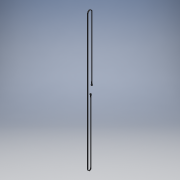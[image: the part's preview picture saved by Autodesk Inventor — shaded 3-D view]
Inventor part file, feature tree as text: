
AUTODESK INVENTOR PART (.ipt)
format: ipt  version: 2017 SP1 (Build 210196100, 196)  size: 156,160 bytes
history: native  units: in
note: dims shown in document units (in); Inventor stores cm internally (conversion verified against a paired STEP export)
features: extrude x1, sketch x1
ambient origin geometry x8: Origin, YZ Plane, XZ Plane, XY Plane, X Axis, Y Axis, Z Axis, Center Point
bodies: Solid1 (feature_tree)
feature tree (2):
  extrude  "Extrusion1"  Depth=0.5in
  sketch  "Sketch1"  dims[d1=0.6875in d2=0.5in d4=0.25in d5=0.0625in d6=2.5in d7=0.25in d8=0.5in d9=0.5in d10=0.005in d11=0.25in d12=0.5in d13=0.005in d14=0.5in d15=47.5in d16=0.375in d17=0.0in]
